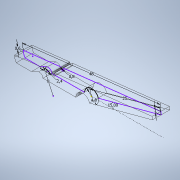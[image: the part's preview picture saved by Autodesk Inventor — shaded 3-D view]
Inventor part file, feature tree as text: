
AUTODESK INVENTOR PART (.ipt)
format: ipt  version: 2022 (Build 260153000, 153)  size: 125,440 bytes
history: native  units: mm
features: other x1, extrude x1, sketch x1
ambient origin geometry x8: Origin, YZ Plane, XZ Plane, XY Plane, X Axis, Y Axis, Z Axis, Center Point
bodies: Body1 (feature_tree)
feature tree (3):
  other  "Těleso1"
  extrude  "Vysunutí1"  Depth=4.8mm
  sketch  "Náčrt1"
